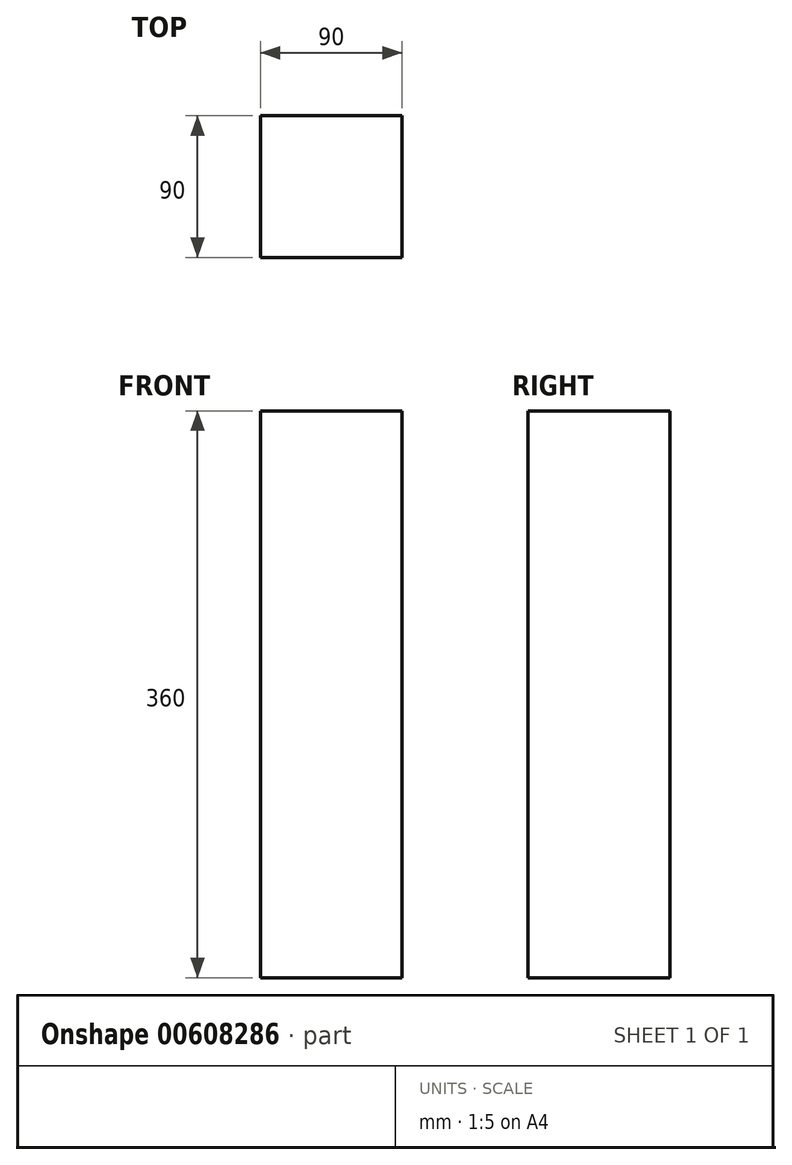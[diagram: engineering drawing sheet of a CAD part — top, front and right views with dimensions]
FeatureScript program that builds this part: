
annotation { "Feature Type Name" : "Feature", "Feature Type Description" : "" }
export const myFeature = defineFeature(function(context is Context, id is Id, definition is map)
    precondition{}
    {
        {
            var Q0;
            Q0=qCreatedBy(makeId("Top.planeOp"),FACE);
            var sketch = newSketch(context, id + "F0", { "sketchPlane" : qUnion([Q0])});
            skLineSegment(sketch, "E0.bottom", {"start": v(0, 0) * mm, "end": v(90, 0) * mm});
            skLineSegment(sketch, "E0.top", {"start": v(0, -90) * mm, "end": v(90, -90) * mm});
            skLineSegment(sketch, "E0.left", {"start": v(0, 0) * mm, "end": v(0, -90) * mm});
            skLineSegment(sketch, "E0.right", {"start": v(90, 0) * mm, "end": v(90, -90) * mm});
            skSolve(sketch);
        }
        {
            var Q0;
            Q0=makeQuery(id+"F0.imprint","IMPRINT",FACE,{"disambiguationData":[TD([[makeQuery(id+"F0.imprint","IMPRINT",EDGE,{"derivedFrom":sQuery(id+"F0.wireOp",EDGE,"E0.bottom")}),-1.0]])]});
            extrude(context, id + "F1", {"entities" : qUnion([Q0]), "depth" : 360 * mm, "offsetDistance" : 25 * mm});
        }
    });
